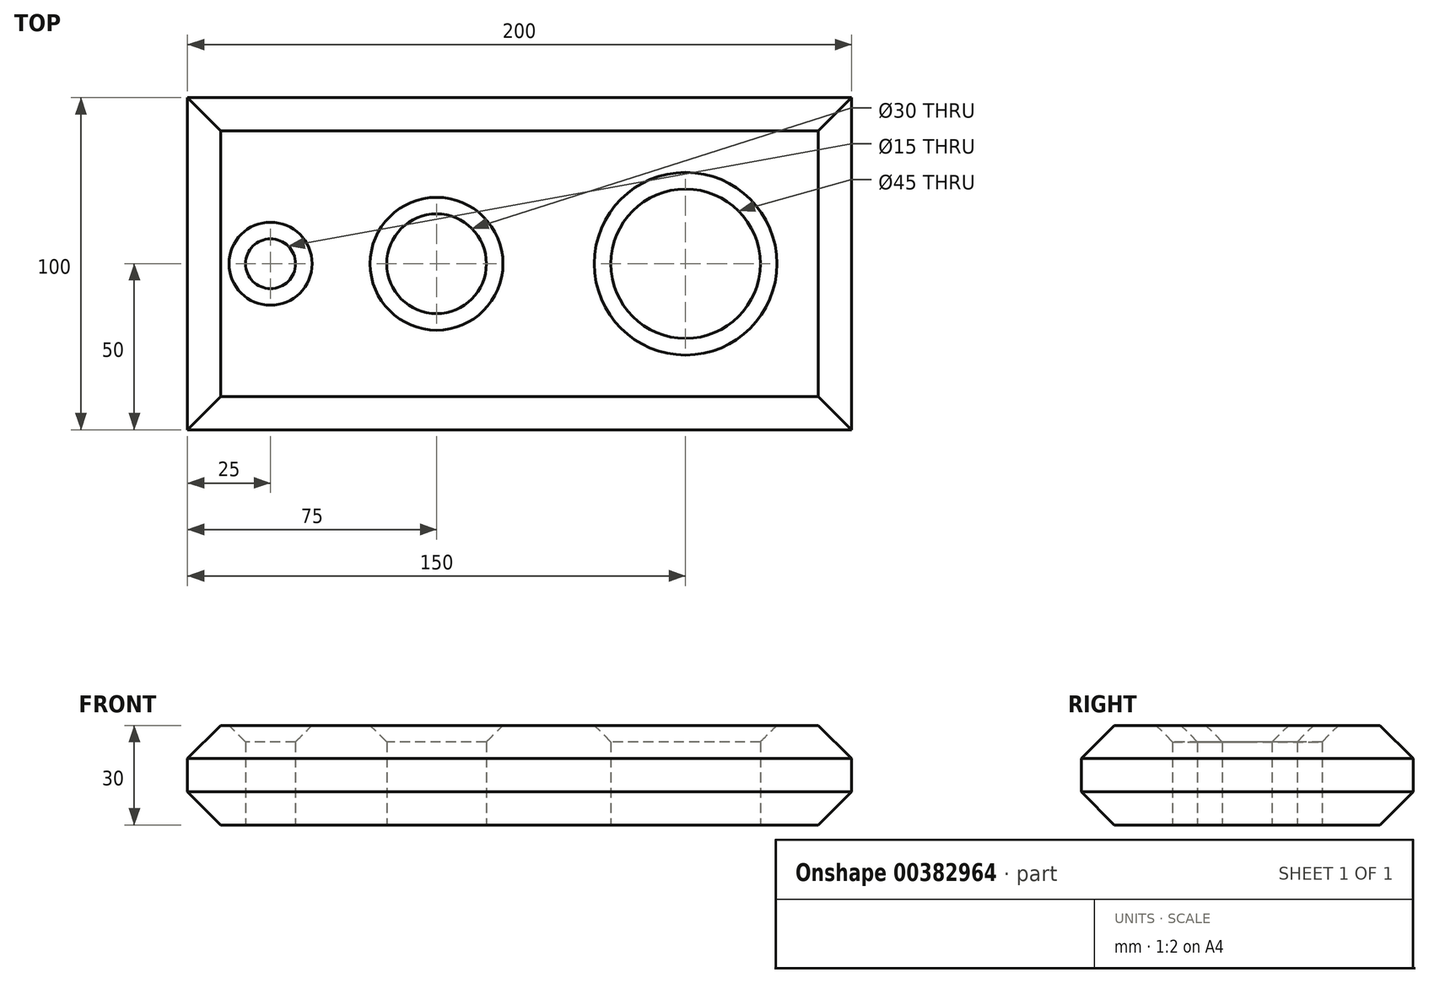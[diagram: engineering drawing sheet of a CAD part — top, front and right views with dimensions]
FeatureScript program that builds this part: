
annotation { "Feature Type Name" : "Feature", "Feature Type Description" : "" }
export const myFeature = defineFeature(function(context is Context, id is Id, definition is map)
    precondition{}
    {
        {
            var Q0;
            Q0=qCreatedBy(makeId("Top.planeOp"),FACE);
            var sketch = newSketch(context, id + "F0", { "sketchPlane" : qUnion([Q0])});
            skLineSegment(sketch, "E0.bottom", {"start": v(100, 50) * mm, "end": v(-100, 50) * mm});
            skLineSegment(sketch, "E0.top", {"start": v(100, -50) * mm, "end": v(-100, -50) * mm});
            skLineSegment(sketch, "E0.left", {"start": v(100, 50) * mm, "end": v(100, -50) * mm});
            skLineSegment(sketch, "E0.right", {"start": v(-100, 50) * mm, "end": v(-100, -50) * mm});
            skPoint(sketch, "E0.middle", {"position": v(0, 0) * mm});
            skLineSegment(sketch, "E1", {"start": v(-100, 0) * mm, "end": v(100, 0) * mm, "construction": true});
            skCircle(sketch, "E2", {"center": v(-75, 0) * mm, "radius": 7.5 * mm});
            skCircle(sketch, "E3", {"center": v(-25, 0) * mm, "radius": 15 * mm});
            skCircle(sketch, "E4", {"center": v(50, 0) * mm, "radius": 22.5 * mm});
            skSolve(sketch);
        }
        {
            var Q0;
            Q0 = qSketchRegion(id + "F0", true);
            extrude(context, id + "F1", {"entities" : qUnion([Q0]), "depth" : 30 * mm});
        }
        {
            var Q0;
            Q0=makeQuery(id+"F1.opExtrude","CAP_EDGE",EDGE,{"disambiguationData":[OSD([sQuery(id+"F0.wireOp",EDGE,"E2")])],"isStart":false});
            var Q1;
            Q1=makeQuery(id+"F1.opExtrude","CAP_EDGE",EDGE,{"disambiguationData":[OSD([sQuery(id+"F0.wireOp",EDGE,"E3")])],"isStart":false});
            var Q2;
            Q2=makeQuery(id+"F1.opExtrude","CAP_EDGE",EDGE,{"disambiguationData":[OSD([sQuery(id+"F0.wireOp",EDGE,"E4")])],"isStart":false});
            chamfer(context, id + "F2", {"entities" : qUnion([Q0, Q1, Q2]), "chamferType" : ChamferType.OFFSET_ANGLE, "width" : 5 * mm, "oppositeDirection" : false, "angle" : 45 * degree, "tangentPropagation" : true});
        }
        {
            var Q0;
            Q0=makeQuery(id+"F1.opExtrude","CAP_EDGE",EDGE,{"disambiguationData":[OSD([sQuery(id+"F0.wireOp",EDGE,"E0.right")])],"isStart":false});
            var Q1;
            Q1=makeQuery(id+"F1.opExtrude","CAP_EDGE",EDGE,{"disambiguationData":[OSD([sQuery(id+"F0.wireOp",EDGE,"E0.right")])],"isStart":true});
            var Q2;
            Q2=makeQuery(id+"F1.opExtrude","CAP_EDGE",EDGE,{"disambiguationData":[OSD([sQuery(id+"F0.wireOp",EDGE,"E0.top")])],"isStart":true});
            var Q3;
            Q3=makeQuery(id+"F1.opExtrude","CAP_EDGE",EDGE,{"disambiguationData":[OSD([sQuery(id+"F0.wireOp",EDGE,"E0.top")])],"isStart":false});
            var Q4;
            Q4=makeQuery(id+"F1.opExtrude","CAP_EDGE",EDGE,{"disambiguationData":[OSD([sQuery(id+"F0.wireOp",EDGE,"E0.left")])],"isStart":true});
            var Q5;
            Q5=makeQuery(id+"F1.opExtrude","CAP_EDGE",EDGE,{"disambiguationData":[OSD([sQuery(id+"F0.wireOp",EDGE,"E0.left")])],"isStart":false});
            var Q6;
            Q6=makeQuery(id+"F1.opExtrude","CAP_EDGE",EDGE,{"disambiguationData":[OSD([sQuery(id+"F0.wireOp",EDGE,"E0.bottom")])],"isStart":true});
            var Q7;
            Q7=makeQuery(id+"F1.opExtrude","CAP_EDGE",EDGE,{"disambiguationData":[OSD([sQuery(id+"F0.wireOp",EDGE,"E0.bottom")])],"isStart":false});
            chamfer(context, id + "F3", {"entities" : qUnion([Q0, Q1, Q2, Q3, Q4, Q5, Q6, Q7]), "chamferType" : ChamferType.OFFSET_ANGLE, "width" : 10 * mm, "oppositeDirection" : false, "angle" : 45 * degree, "tangentPropagation" : true});
        }
    });
